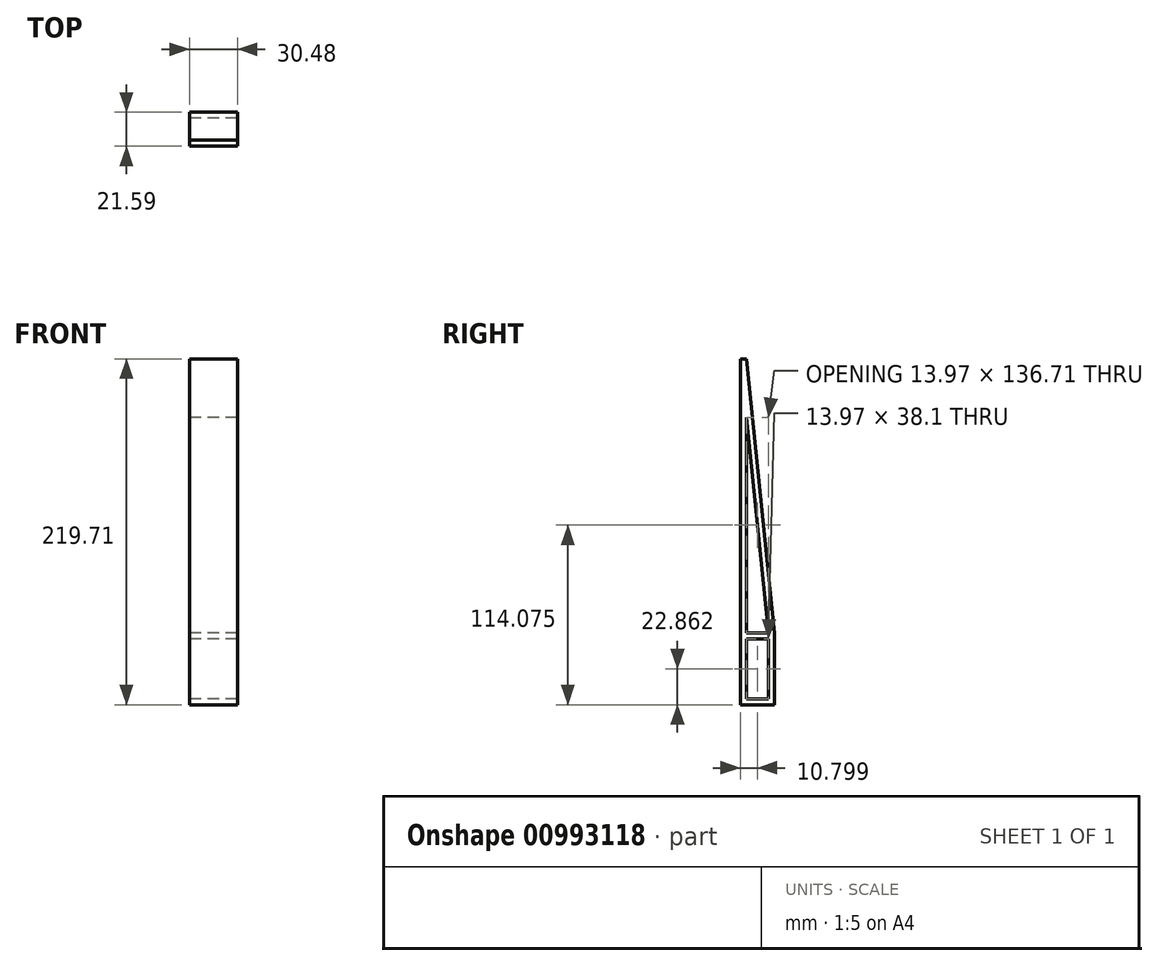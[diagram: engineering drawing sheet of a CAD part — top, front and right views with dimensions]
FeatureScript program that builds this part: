
annotation { "Feature Type Name" : "Feature", "Feature Type Description" : "" }
export const myFeature = defineFeature(function(context is Context, id is Id, definition is map)
    precondition{}
    {
        {
            var Q0;
            Q0=qCreatedBy(makeId("Right.planeOp"),FACE);
            var sketch = newSketch(context, id + "F0", { "sketchPlane" : qUnion([Q0])});
            skLineSegment(sketch, "E0", {"start": v(-38.44, 112.5) * mm, "end": v(-38.44, -107.2) * mm});
            skLineSegment(sketch, "E1.bottom", {"start": v(-38.44, 112.5) * mm, "end": v(-34.63, 112.5) * mm});
            skLineSegment(sketch, "E1.top", {"start": v(-38.44, -107.2) * mm, "end": v(-34.63, -107.2) * mm});
            skLineSegment(sketch, "E1.right", {"start": v(-34.63, 112.5) * mm, "end": v(-34.63, -107.2) * mm});
            skLineSegment(sketch, "E2.bottom", {"start": v(-34.63, -61.49) * mm, "end": v(-16.85, -61.49) * mm});
            skLineSegment(sketch, "E2.top", {"start": v(-34.63, -107.2) * mm, "end": v(-16.85, -107.2) * mm});
            skLineSegment(sketch, "E2.left", {"start": v(-34.63, -61.49) * mm, "end": v(-34.63, -107.2) * mm});
            skLineSegment(sketch, "E2.right", {"start": v(-16.85, -61.49) * mm, "end": v(-16.85, -107.2) * mm});
            skLineSegment(sketch, "E3", {"start": v(-34.63, 112.5) * mm, "end": v(-16.85, -61.49) * mm});
            skLineSegment(sketch, "E4", {"start": v(-20.66, -61.49) * mm, "end": v(-34.63, 75.22) * mm});
            skLineSegment(sketch, "E5.bottom", {"start": v(-20.66, -65.3) * mm, "end": v(-34.63, -65.3) * mm});
            skLineSegment(sketch, "E5.top", {"start": v(-20.66, -103.4) * mm, "end": v(-34.63, -103.4) * mm});
            skLineSegment(sketch, "E5.left", {"start": v(-20.66, -65.3) * mm, "end": v(-20.66, -103.4) * mm});
            skLineSegment(sketch, "E5.right", {"start": v(-34.63, -65.3) * mm, "end": v(-34.63, -103.4) * mm});
            skSolve(sketch);
        }
        {
            var Q0;
            {var subQ0=sQuery(id+"F0.wireOp",EDGE,"E3");Q0=makeQuery(id+"F0.imprint","IMPRINT",FACE,{"disambiguationData":[TD([[makeQuery(id+"F0.imprint","IMPRINT",EDGE,{"derivedFrom":subQ0}),-1.0]])]});}
            var Q1;
            {var subQ1=sQuery(id+"F0.wireOp",EDGE,"E1.bottom");Q1=makeQuery(id+"F0.imprint","IMPRINT",FACE,{"disambiguationData":[TD([[makeQuery(id+"F0.imprint","IMPRINT",EDGE,{"derivedFrom":subQ1}),-1.0]])]});}
            var Q2;
            {var subQ5=sQuery(id+"F0.wireOp",EDGE,"E2.top");Q2=makeQuery(id+"F0.imprint","IMPRINT",FACE,{"disambiguationData":[TD([[makeQuery(id+"F0.imprint","IMPRINT",EDGE,{"derivedFrom":subQ5}),1.0]])]});}
            extrude(context, id + "F1", {"entities" : qUnion([Q0, Q1, Q2]), "depth" : 30.48 * mm, "offsetDistance" : 25.4 * mm});
        }
    });
